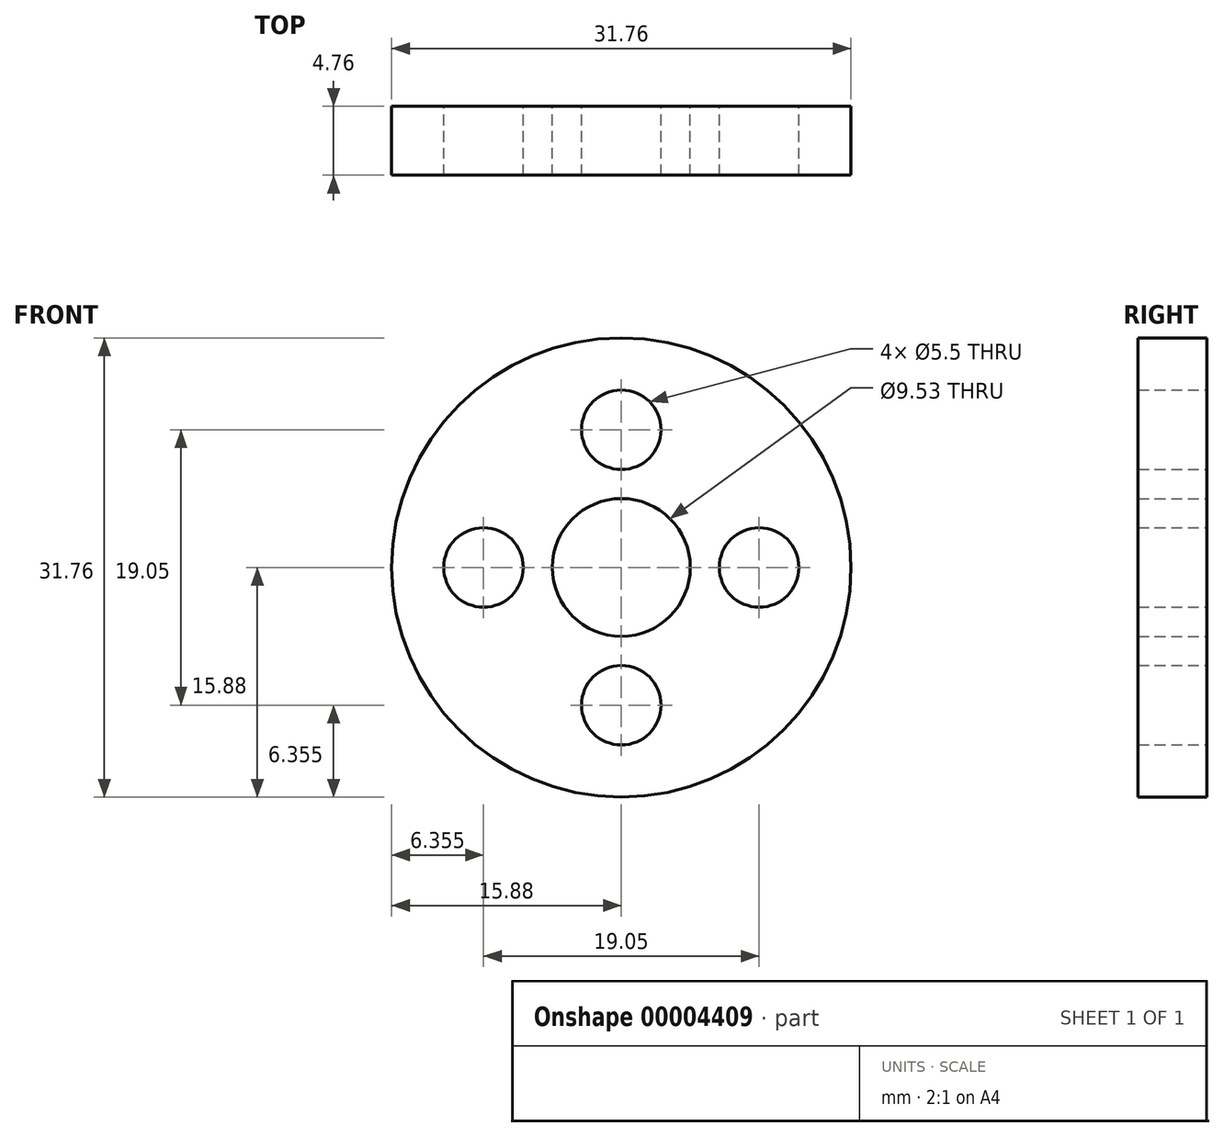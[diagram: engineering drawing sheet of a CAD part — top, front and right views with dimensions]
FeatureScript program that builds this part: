
annotation { "Feature Type Name" : "Feature", "Feature Type Description" : "" }
export const myFeature = defineFeature(function(context is Context, id is Id, definition is map)
    precondition{}
    {
        {
            var Q0;
            Q0=qCreatedBy(makeId("Front.planeOp"),FACE);
            var sketch = newSketch(context, id + "F0", { "sketchPlane" : qUnion([Q0])});
            skCircle(sketch, "E0", {"center": v(0, 0) * mm, "radius": 15.88 * mm});
            skCircle(sketch, "E1", {"center": v(0, 0) * mm, "radius": 4.76 * mm});
            skCircle(sketch, "E2", {"center": v(0, 0) * mm, "radius": 9.53 * mm, "construction": true});
            skCircle(sketch, "E3", {"center": v(0, 9.53) * mm, "radius": 2.75 * mm});
            skCircle(sketch, "E4", {"center": v(-9.53, 0) * mm, "radius": 2.75 * mm});
            skCircle(sketch, "E5", {"center": v(0, -9.53) * mm, "radius": 2.75 * mm});
            skCircle(sketch, "E6", {"center": v(9.53, 0) * mm, "radius": 2.75 * mm});
            skSolve(sketch);
        }
        {
            var Q0;
            Q0=makeQuery(id+"F0.imprint","IMPRINT",FACE,{"disambiguationData":[TD([[makeQuery(id+"F0.imprint","IMPRINT",EDGE,{"derivedFrom":sQuery(id+"F0.wireOp",EDGE,"E0")}),1.0]])]});
            extrude(context, id + "F1", {"entities" : qUnion([Q0]), "depth" : 4.76 * mm});
        }
    });
